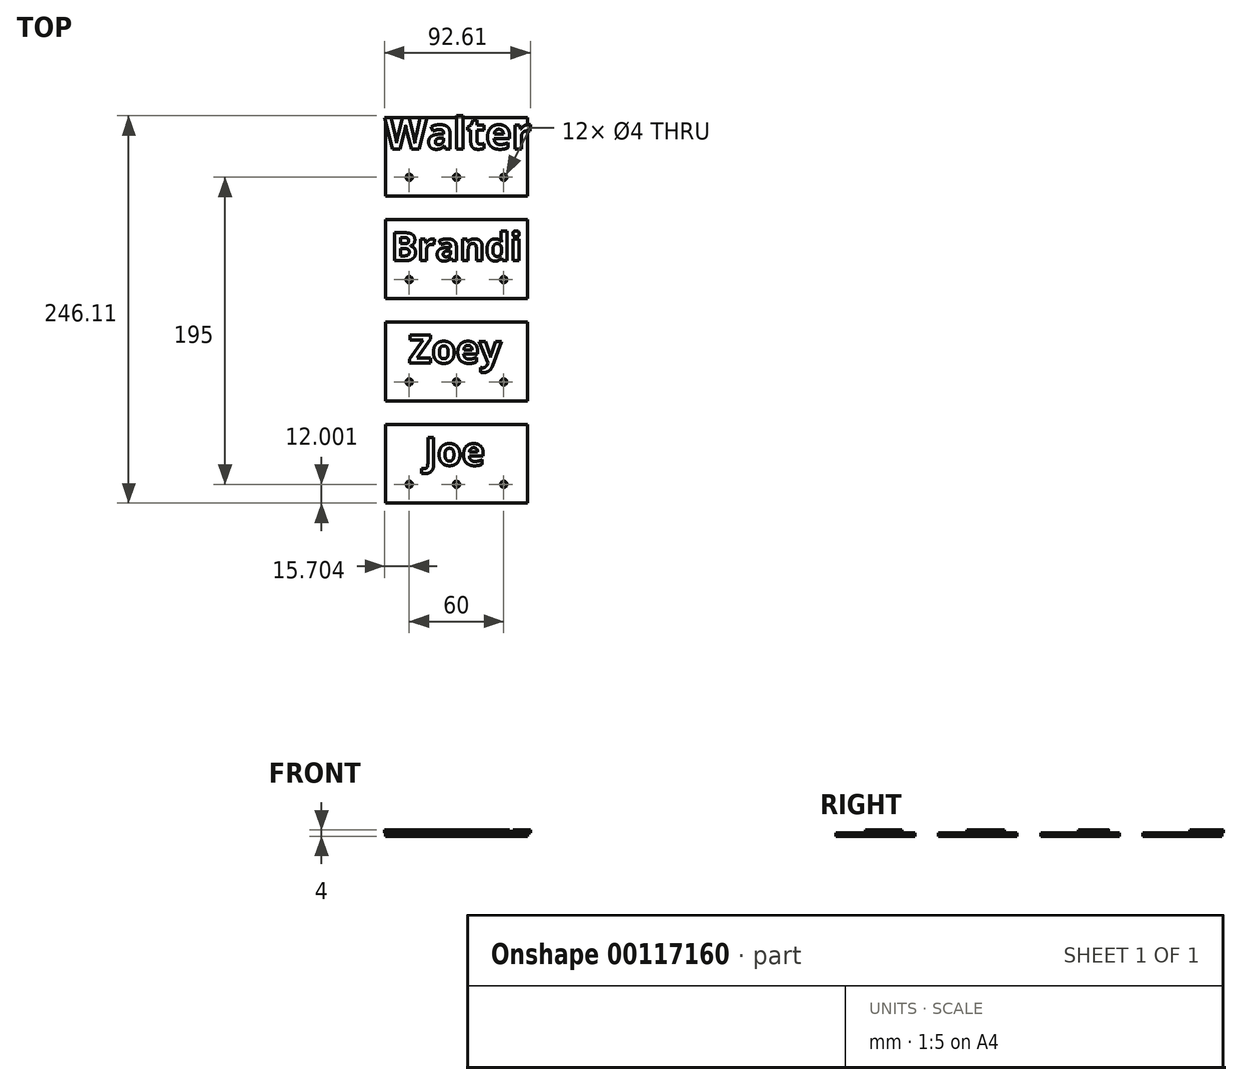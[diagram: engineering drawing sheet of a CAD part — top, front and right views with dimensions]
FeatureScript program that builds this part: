
annotation { "Feature Type Name" : "Feature", "Feature Type Description" : "" }
export const myFeature = defineFeature(function(context is Context, id is Id, definition is map)
    precondition{}
    {
        {
            var Q0;
            Q0=qCreatedBy(makeId("Top.planeOp"),FACE);
            var sketch = newSketch(context, id + "F0", { "sketchPlane" : qUnion([Q0])});
            skLineSegment(sketch, "E0.bottom", {"start": v(-49.16, 45.68) * mm, "end": v(40.84, 45.68) * mm});
            skLineSegment(sketch, "E0.top", {"start": v(-49.16, -4.32) * mm, "end": v(40.84, -4.32) * mm});
            skLineSegment(sketch, "E0.left", {"start": v(-49.16, 45.68) * mm, "end": v(-49.16, -4.32) * mm});
            skLineSegment(sketch, "E0.right", {"start": v(40.84, 45.68) * mm, "end": v(40.84, -4.32) * mm});
            skLineSegment(sketch, "E1", {"start": v(-49.16, 7.68) * mm, "end": v(40.84, 7.68) * mm, "construction": true});
            skLineSegment(sketch, "E2", {"start": v(-49.16, 19.68) * mm, "end": v(40.84, 19.68) * mm, "construction": true});
            skLineSegment(sketch, "E3", {"start": v(-4.16, -4.32) * mm, "end": v(-4.16, 45.68) * mm, "construction": true});
            skCircle(sketch, "E4", {"center": v(-4.16, 7.68) * mm, "radius": 2 * mm});
            skCircle(sketch, "E5", {"center": v(-34.16, 7.68) * mm, "radius": 2 * mm});
            skCircle(sketch, "E6.MirrorC", {"center": v(25.84, 7.68) * mm, "radius": 2 * mm});
            skLineSegment(sketch, "E7.0.1.0", {"start": v(-49.16, -19.32) * mm, "end": v(40.84, -19.32) * mm});
            skLineSegment(sketch, "E7.0.1.1", {"start": v(-49.16, -69.32) * mm, "end": v(40.84, -69.32) * mm});
            skLineSegment(sketch, "E7.0.1.2", {"start": v(-49.16, -19.32) * mm, "end": v(-49.16, -69.32) * mm});
            skLineSegment(sketch, "E7.0.1.3", {"start": v(40.84, -19.32) * mm, "end": v(40.84, -69.32) * mm});
            skLineSegment(sketch, "E7.0.1.4", {"start": v(-49.16, -57.32) * mm, "end": v(40.84, -57.32) * mm, "construction": true});
            skLineSegment(sketch, "E7.0.1.5", {"start": v(-49.16, -45.32) * mm, "end": v(40.84, -45.32) * mm, "construction": true});
            skLineSegment(sketch, "E7.0.1.6", {"start": v(-4.16, -69.32) * mm, "end": v(-4.16, -19.32) * mm, "construction": true});
            skCircle(sketch, "E7.0.1.7", {"center": v(-34.16, -57.32) * mm, "radius": 2 * mm});
            skCircle(sketch, "E7.0.1.8", {"center": v(25.84, -57.32) * mm, "radius": 2 * mm});
            skCircle(sketch, "E7.0.1.9", {"center": v(-4.16, -57.32) * mm, "radius": 2 * mm});
            skCircle(sketch, "E7.0.1.10", {"center": v(25.84, -57.32) * mm, "radius": 2 * mm});
            skCircle(sketch, "E7.0.1.11", {"center": v(-4.16, -57.32) * mm, "radius": 2 * mm});
            skLineSegment(sketch, "E7.0.2.0", {"start": v(-49.16, -84.32) * mm, "end": v(40.84, -84.32) * mm});
            skLineSegment(sketch, "E7.0.2.1", {"start": v(-49.16, -134.32) * mm, "end": v(40.84, -134.32) * mm});
            skLineSegment(sketch, "E7.0.2.2", {"start": v(-49.16, -84.32) * mm, "end": v(-49.16, -134.32) * mm});
            skLineSegment(sketch, "E7.0.2.3", {"start": v(40.84, -84.32) * mm, "end": v(40.84, -134.32) * mm});
            skLineSegment(sketch, "E7.0.2.4", {"start": v(-49.16, -122.32) * mm, "end": v(40.84, -122.32) * mm, "construction": true});
            skLineSegment(sketch, "E7.0.2.5", {"start": v(-49.16, -110.32) * mm, "end": v(40.84, -110.32) * mm, "construction": true});
            skLineSegment(sketch, "E7.0.2.6", {"start": v(-4.16, -134.32) * mm, "end": v(-4.16, -84.32) * mm, "construction": true});
            skCircle(sketch, "E7.0.2.7", {"center": v(-34.16, -122.32) * mm, "radius": 2 * mm});
            skCircle(sketch, "E7.0.2.8", {"center": v(25.84, -122.32) * mm, "radius": 2 * mm});
            skCircle(sketch, "E7.0.2.9", {"center": v(-4.16, -122.32) * mm, "radius": 2 * mm});
            skCircle(sketch, "E7.0.2.10", {"center": v(25.84, -122.32) * mm, "radius": 2 * mm});
            skCircle(sketch, "E7.0.2.11", {"center": v(-4.16, -122.32) * mm, "radius": 2 * mm});
            skLineSegment(sketch, "E7.0.3.0", {"start": v(-49.16, -149.32) * mm, "end": v(40.84, -149.32) * mm});
            skLineSegment(sketch, "E7.0.3.1", {"start": v(-49.16, -199.32) * mm, "end": v(40.84, -199.32) * mm});
            skLineSegment(sketch, "E7.0.3.2", {"start": v(-49.16, -149.32) * mm, "end": v(-49.16, -199.32) * mm});
            skLineSegment(sketch, "E7.0.3.3", {"start": v(40.84, -149.32) * mm, "end": v(40.84, -199.32) * mm});
            skLineSegment(sketch, "E7.0.3.4", {"start": v(-49.16, -187.32) * mm, "end": v(40.84, -187.32) * mm, "construction": true});
            skLineSegment(sketch, "E7.0.3.5", {"start": v(-49.16, -175.32) * mm, "end": v(40.84, -175.32) * mm, "construction": true});
            skLineSegment(sketch, "E7.0.3.6", {"start": v(-4.16, -199.32) * mm, "end": v(-4.16, -149.32) * mm, "construction": true});
            skCircle(sketch, "E7.0.3.7", {"center": v(-34.16, -187.32) * mm, "radius": 2 * mm});
            skCircle(sketch, "E7.0.3.8", {"center": v(25.84, -187.32) * mm, "radius": 2 * mm});
            skCircle(sketch, "E7.0.3.9", {"center": v(-4.16, -187.32) * mm, "radius": 2 * mm});
            skCircle(sketch, "E7.0.3.10", {"center": v(25.84, -187.32) * mm, "radius": 2 * mm});
            skCircle(sketch, "E7.0.3.11", {"center": v(-4.16, -187.32) * mm, "radius": 2 * mm});
            skLineSegment(sketch, "E7.direction1", {"start": v(-49.16, -4.32) * mm, "end": v(-37.66, -4.32) * mm, "construction": true});
            skLineSegment(sketch, "E7.direction2", {"start": v(-49.16, -4.32) * mm, "end": v(-49.16, -69.32) * mm, "construction": true});
            skLineSegment(sketch, "E8", {"start": v(-49.16, 37.68) * mm, "end": v(40.84, 37.68) * mm, "construction": true});
            skSolve(sketch);
        }
        {
            var Q0;
            Q0=makeQuery(id+"F0.imprint","IMPRINT",FACE,{"disambiguationData":[TD([[makeQuery(id+"F0.imprint","IMPRINT",EDGE,{"derivedFrom":sQuery(id+"F0.wireOp",EDGE,"E0.bottom")}),-1.0]])]});
            var Q1;
            Q1=makeQuery(id+"F0.imprint","IMPRINT",FACE,{"disambiguationData":[TD([[makeQuery(id+"F0.imprint","IMPRINT",EDGE,{"derivedFrom":sQuery(id+"F0.wireOp",EDGE,"E7.0.1.0")}),-1.0]])]});
            var Q2;
            Q2=makeQuery(id+"F0.imprint","IMPRINT",FACE,{"disambiguationData":[TD([[makeQuery(id+"F0.imprint","IMPRINT",EDGE,{"derivedFrom":sQuery(id+"F0.wireOp",EDGE,"E7.0.2.0")}),-1.0]])]});
            var Q3;
            Q3=makeQuery(id+"F0.imprint","IMPRINT",FACE,{"disambiguationData":[TD([[makeQuery(id+"F0.imprint","IMPRINT",EDGE,{"derivedFrom":sQuery(id+"F0.wireOp",EDGE,"E7.0.3.0")}),-1.0]])]});
            extrude(context, id + "F1", {"entities" : qUnion([Q0, Q1, Q2, Q3]), "oppositeDirection" : true, "depth" : 2 * mm});
        }
        {
            var Q0;
            Q0=makeQuery(id+"F1.opExtrude","CAP_FACE",FACE,{"disambiguationData":[OSD([sQuery(id+"F0.wireOp",EDGE,"E0.bottom"),sQuery(id+"F0.wireOp",EDGE,"E0.top"),sQuery(id+"F0.wireOp",EDGE,"E0.left"),sQuery(id+"F0.wireOp",EDGE,"E0.right"),sQuery(id+"F0.wireOp",EDGE,"E5"),sQuery(id+"F0.wireOp",EDGE,"E4"),sQuery(id+"F0.wireOp",EDGE,"E6.MirrorC")])],"isStart":true});
            var sketch = newSketch(context, id + "F2", { "sketchPlane" : qUnion([Q0])});
            skText(sketch, "E9", { "text": "Walter", "fontName": "OpenSans-Bold.ttf"});
            skLineSegment(sketch, "E10.0", {"start": v(-49.16, 19.68) * mm, "end": v(40.84, 19.68) * mm, "construction": true});
            const initialGuessF2  = {"E9": [-0.04986, 0.02568, 1, 0, 0.02]};
            skSetInitialGuess(sketch, initialGuessF2);
            skSolve(sketch);
        }
        {
            var Q0;
            Q0 = qSketchRegion(id + "F2", true);
            extrude(context, id + "F3", {"entities" : qUnion([Q0]), "operationType" : NewBodyOperationType.ADD, "depth" : 2 * mm});
        }
        {
            var Q0;
            Q0=makeQuery(id+"F0.imprint","IMPRINT",FACE,{"disambiguationData":[TD([[makeQuery(id+"F0.imprint","IMPRINT",EDGE,{"derivedFrom":sQuery(id+"F0.wireOp",EDGE,"E7.0.1.0")}),-1.0]])]});
            var sketch = newSketch(context, id + "F4", { "sketchPlane" : qUnion([Q0])});
            skText(sketch, "E11", { "text": "Brandi", "fontName": "OpenSans-Bold.ttf"});
            const initialGuessF4  = {"E11": [-0.04564, -0.04532, 1, 0, 0.018]};
            skSetInitialGuess(sketch, initialGuessF4);
            skSolve(sketch);
        }
        {
            var Q0;
            Q0 = qSketchRegion(id + "F4", true);
            extrude(context, id + "F5", {"entities" : qUnion([Q0]), "operationType" : NewBodyOperationType.ADD, "depth" : 2 * mm});
        }
        {
            var Q0;
            Q0=makeQuery(id+"F0.imprint","IMPRINT",FACE,{"disambiguationData":[TD([[makeQuery(id+"F0.imprint","IMPRINT",EDGE,{"derivedFrom":sQuery(id+"F0.wireOp",EDGE,"E7.0.2.0")}),-1.0]])]});
            var sketch = newSketch(context, id + "F6", { "sketchPlane" : qUnion([Q0])});
            skText(sketch, "E12", { "text": "Zoey", "fontName": "OpenSans-Bold.ttf"});
            const initialGuessF6  = {"E12": [-0.03444, -0.11032, 1, 0, 0.018]};
            skSetInitialGuess(sketch, initialGuessF6);
            skSolve(sketch);
        }
        {
            var Q0;
            Q0 = qSketchRegion(id + "F6", true);
            extrude(context, id + "F7", {"entities" : qUnion([Q0]), "operationType" : NewBodyOperationType.ADD, "depth" : 2 * mm});
        }
        {
            var Q0;
            Q0=makeQuery(id+"F0.imprint","IMPRINT",FACE,{"disambiguationData":[TD([[makeQuery(id+"F0.imprint","IMPRINT",EDGE,{"derivedFrom":sQuery(id+"F0.wireOp",EDGE,"E7.0.3.0")}),-1.0]])]});
            var sketch = newSketch(context, id + "F8", { "sketchPlane" : qUnion([Q0])});
            skText(sketch, "E13", { "text": "Joe", "fontName": "OpenSans-Bold.ttf"});
            const initialGuessF8  = {"E13": [-0.02462, -0.17532, 1, 0, 0.018]};
            skSetInitialGuess(sketch, initialGuessF8);
            skSolve(sketch);
        }
        {
            var Q0;
            Q0 = qSketchRegion(id + "F8", true);
            extrude(context, id + "F9", {"entities" : qUnion([Q0]), "operationType" : NewBodyOperationType.ADD, "depth" : 2 * mm});
        }
    });
